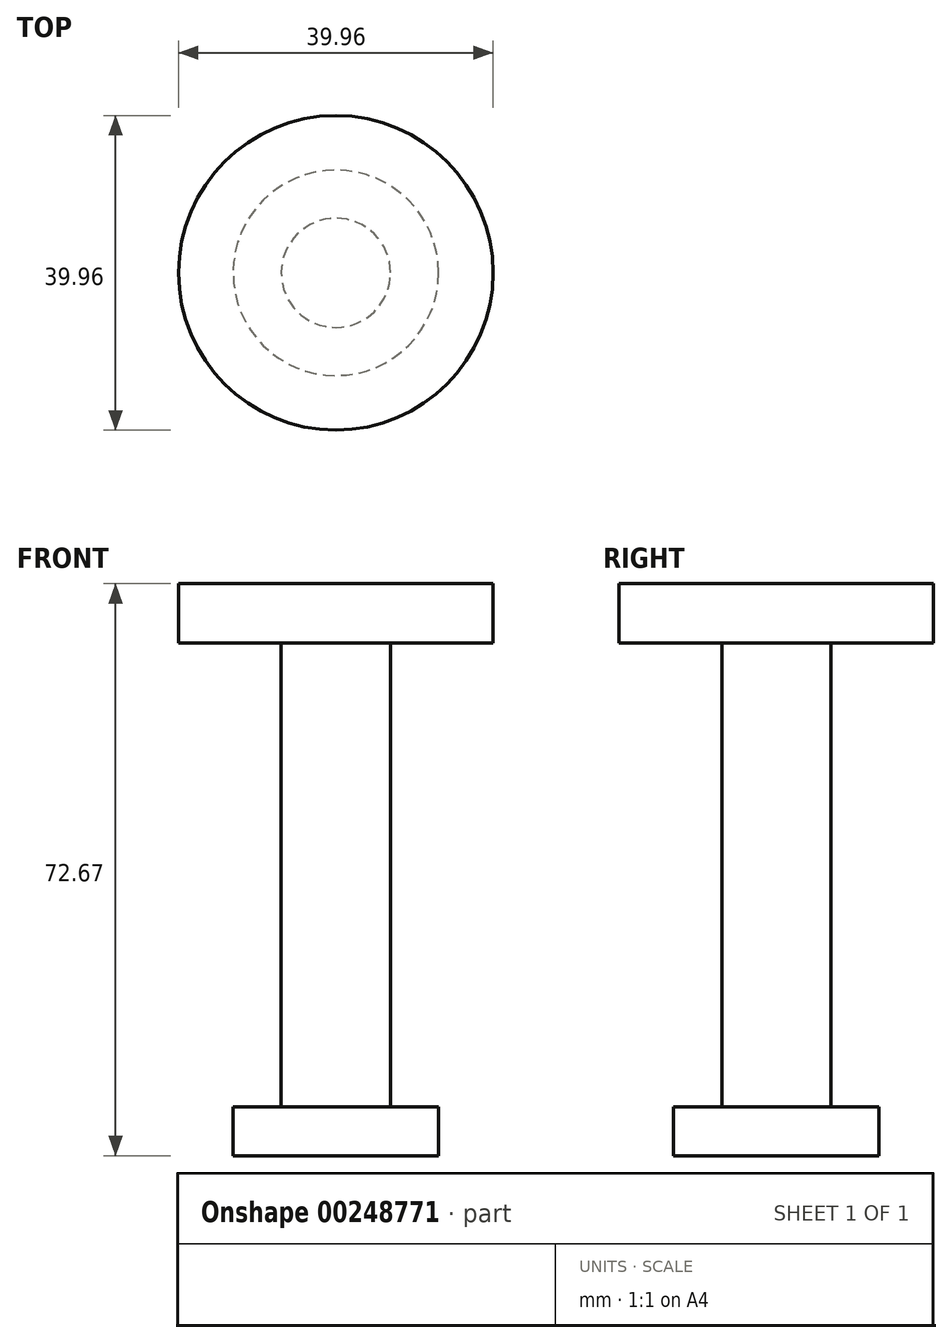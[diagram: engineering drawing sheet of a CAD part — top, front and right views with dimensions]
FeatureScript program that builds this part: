
annotation { "Feature Type Name" : "Feature", "Feature Type Description" : "" }
export const myFeature = defineFeature(function(context is Context, id is Id, definition is map)
    precondition{}
    {
        {
            var Q0;
            Q0=qCreatedBy(makeId("Front.planeOp"),FACE);
            var sketch = newSketch(context, id + "F0", { "sketchPlane" : qUnion([Q0])});
            skLineSegment(sketch, "E0", {"start": v(13.05, 0) * mm, "end": v(13.05, 6.22) * mm});
            skLineSegment(sketch, "E1", {"start": v(13.05, 6.22) * mm, "end": v(6.93, 6.22) * mm});
            skLineSegment(sketch, "E2", {"start": v(6.93, 6.22) * mm, "end": v(6.93, 65.13) * mm});
            skLineSegment(sketch, "E3", {"start": v(6.93, 65.13) * mm, "end": v(19.98, 65.13) * mm});
            skLineSegment(sketch, "E4", {"start": v(19.98, 65.13) * mm, "end": v(19.98, 72.67) * mm});
            skLineSegment(sketch, "E5", {"start": v(19.98, 72.67) * mm, "end": v(0, 72.67) * mm});
            skLineSegment(sketch, "E6", {"start": v(0, 72.67) * mm, "end": v(0, 0) * mm});
            skLineSegment(sketch, "E7", {"start": v(0, -50.13) * mm, "end": v(0, 89.24) * mm, "construction": true});
            skLineSegment(sketch, "E8", {"start": v(13.05, 0) * mm, "end": v(0, 0) * mm});
            skSolve(sketch);
        }
        {
            var Q0;
            Q0 = qSketchRegion(id + "F0", true);
            var Q1;
            Q1=sQuery(id+"F0.wireOp",EDGE,"E7");
            revolve(context, id + "F1", {"entities" : qUnion([Q0]), "axis" : qUnion([Q1]), "revolveType" : RevolveType.FULL});
        }
    });
